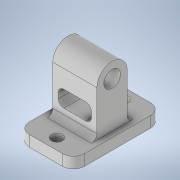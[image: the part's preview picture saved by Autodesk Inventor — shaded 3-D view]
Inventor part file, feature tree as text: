
AUTODESK INVENTOR PART (.ipt)
format: ipt  version: 2021 (Build 250183000, 183)  size: 175,616 bytes
history: native  units: mm
features: sketch x5, fillet x4, extrude x3, hole x2, other x1
ambient origin geometry x8: Origin, YZ Plane, XZ Plane, XY Plane, X Axis, Y Axis, Z Axis, Center Point
bodies: Body1 (feature_tree)
feature tree (15):
  other  "Sólido1"
  extrude  "Extrusão1"  Depth=160.0mm
  extrude  "Extrusão2"  Depth=55.0mm
  fillet  "Arredondamento1"  Radius=80.0mm
  hole  "Furo1"  [1 undecoded]
  extrude  "Extrusão3"  Depth=60.0mm
  hole  "Furo2"  [1 undecoded]
  fillet  "Arredondamento2"  [1 undecoded]
  fillet  "Arredondamento3"  Radius=20.0mm
  fillet  "Arredondamento4"  Radius=50.0mm
  sketch  "Esboço1"  dims[d0=100.0mm d1=160.0mm]
  sketch  "Esboço2"  dims[d2=20.0mm d3=0.0mm d4=55.0mm d5=80.0mm]
  sketch  "Esboço3"  dims[d6=110.0mm d7=0.0mm d8=27.5mm]
  sketch  "Esboço4"  dims[d9=30.0mm d10=6.0mm d11=4.0mm d12=2.0mm d13=90.0deg d14=8.0mm d15=20.594885mm d18=60.0mm]
  sketch  "Esboço5"  dims[d19=55.0mm d20=30.0mm d21=0.0mm d22=0.0mm d23=20.0mm d24=50.0mm d25=20.0mm d26=50.0mm d27=20.0mm d28=6.0mm d29=4.0mm d30=2.0mm d31=90.0deg d32=8.0mm d33=20.594885mm d34=10.0mm d35=10.0mm d36=20.0mm d37=0.5mm d38=0.872665mm d39=0.5mm d40=0.872665mm]
note: 3 required parameter values undecoded (feature->parameter linkage not recoverable at this tier; creation-order binding heuristic only, values carry confidence <= 0.55)
